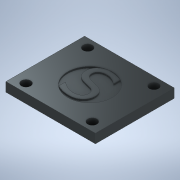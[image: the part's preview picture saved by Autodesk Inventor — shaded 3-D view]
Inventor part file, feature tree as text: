
AUTODESK INVENTOR PART (.ipt)
format: ipt  version: 2020 (Build 240168000, 168)  size: 179,200 bytes
history: native  units: mm
features: extrude x4, sketch x4
ambient origin geometry x8: Origin, YZ Plane, XZ Plane, XY Plane, X Axis, Y Axis, Z Axis, Center Point
bodies: Solid1 (feature_tree)
feature tree (8):
  extrude  "Extrusion1"  Depth=25.5mm
  sketch  "Sketch2"  dims[d2=3.0mm d3=0.0mm d4=3.0mm]
  sketch  "Sketch3"  dims[d5=2.75mm d6=3.75mm]
  extrude  "Extrusion2"  Depth=3.0mm
  sketch  "Sketch4"  dims[d7=20.0mm d9=21.5mm d10=20.0mm d12=20.0mm d15=14.5mm d16=0.0mm d17=0.0mm d18=0.5mm d19=0.0mm d20=0.5mm d21=0.0mm]
  extrude  "Extrusion3"  Depth=3.75mm
  extrude  "Extrusion4"  Depth=14.5mm
  sketch  "Sketch1"  dims[d0=29.0mm d1=25.5mm]
